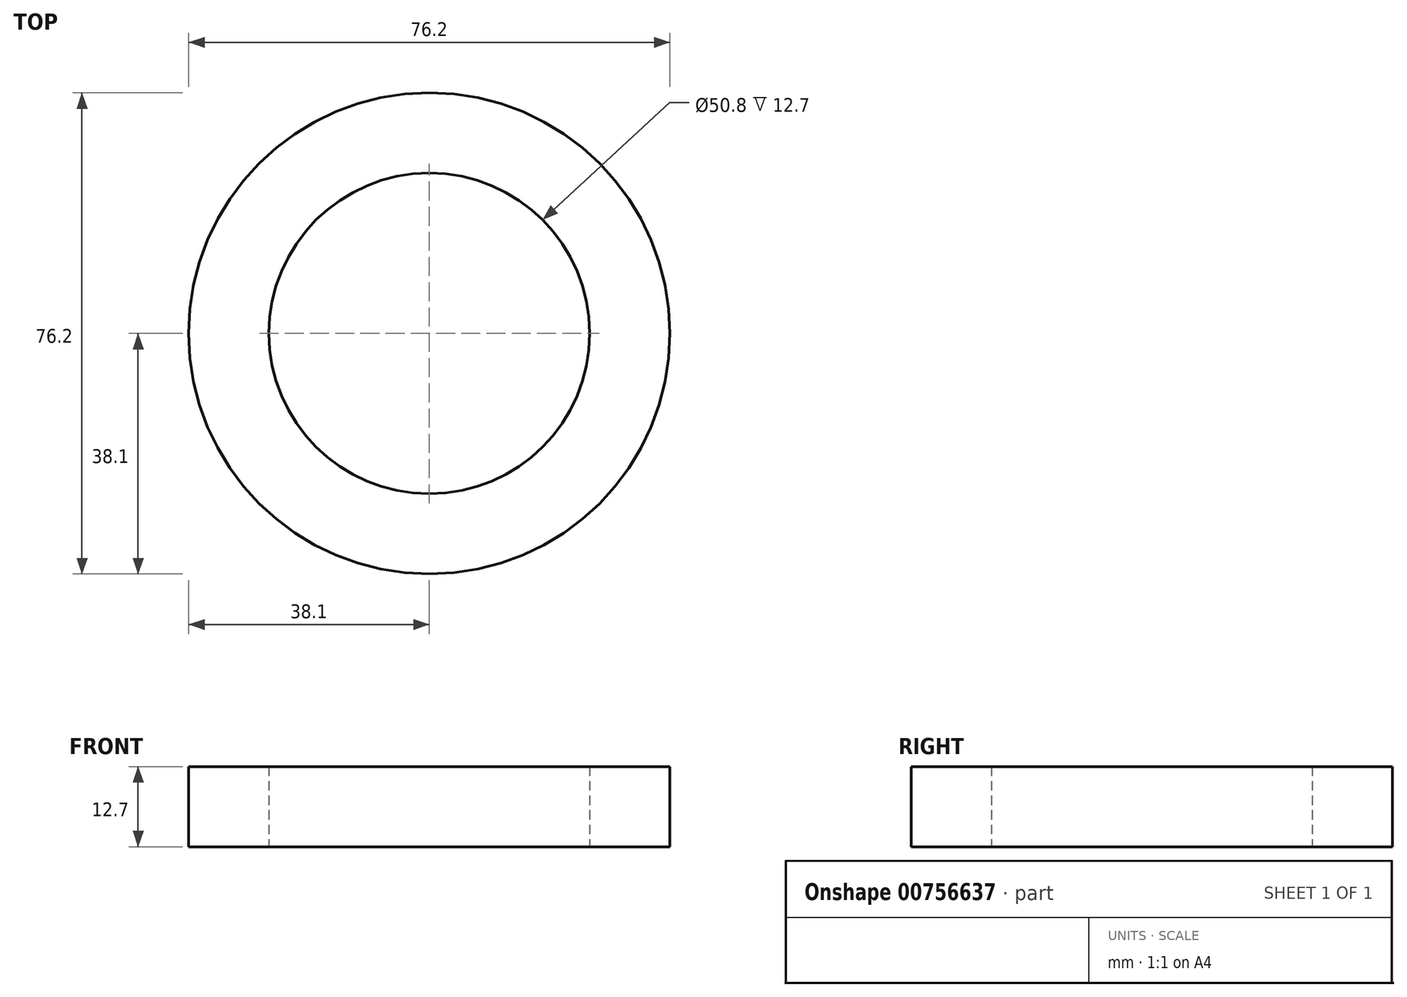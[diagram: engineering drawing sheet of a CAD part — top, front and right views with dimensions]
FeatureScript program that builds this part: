
annotation { "Feature Type Name" : "Feature", "Feature Type Description" : "" }
export const myFeature = defineFeature(function(context is Context, id is Id, definition is map)
    precondition{}
    {
        {
            var Q0;
            Q0=qCreatedBy(makeId("Top.planeOp"),FACE);
            var sketch = newSketch(context, id + "F0", { "sketchPlane" : qUnion([Q0])});
            skCircle(sketch, "E0", {"center": v(0, 0) * mm, "radius": 25.4 * mm});
            skCircle(sketch, "E1", {"center": v(0, 0) * mm, "radius": 38.1 * mm});
            skSolve(sketch);
        }
        {
            var Q0;
            Q0=makeQuery(id+"F0.imprint","IMPRINT",FACE,{"disambiguationData":[TD([[makeQuery(id+"F0.imprint","IMPRINT",EDGE,{"derivedFrom":sQuery(id+"F0.wireOp",EDGE,"E0")}),-1.0]])]});
            extrude(context, id + "F1", {"entities" : qUnion([Q0]), "depth" : 12.7 * mm, "offsetDistance" : 25.4 * mm});
        }
    });
